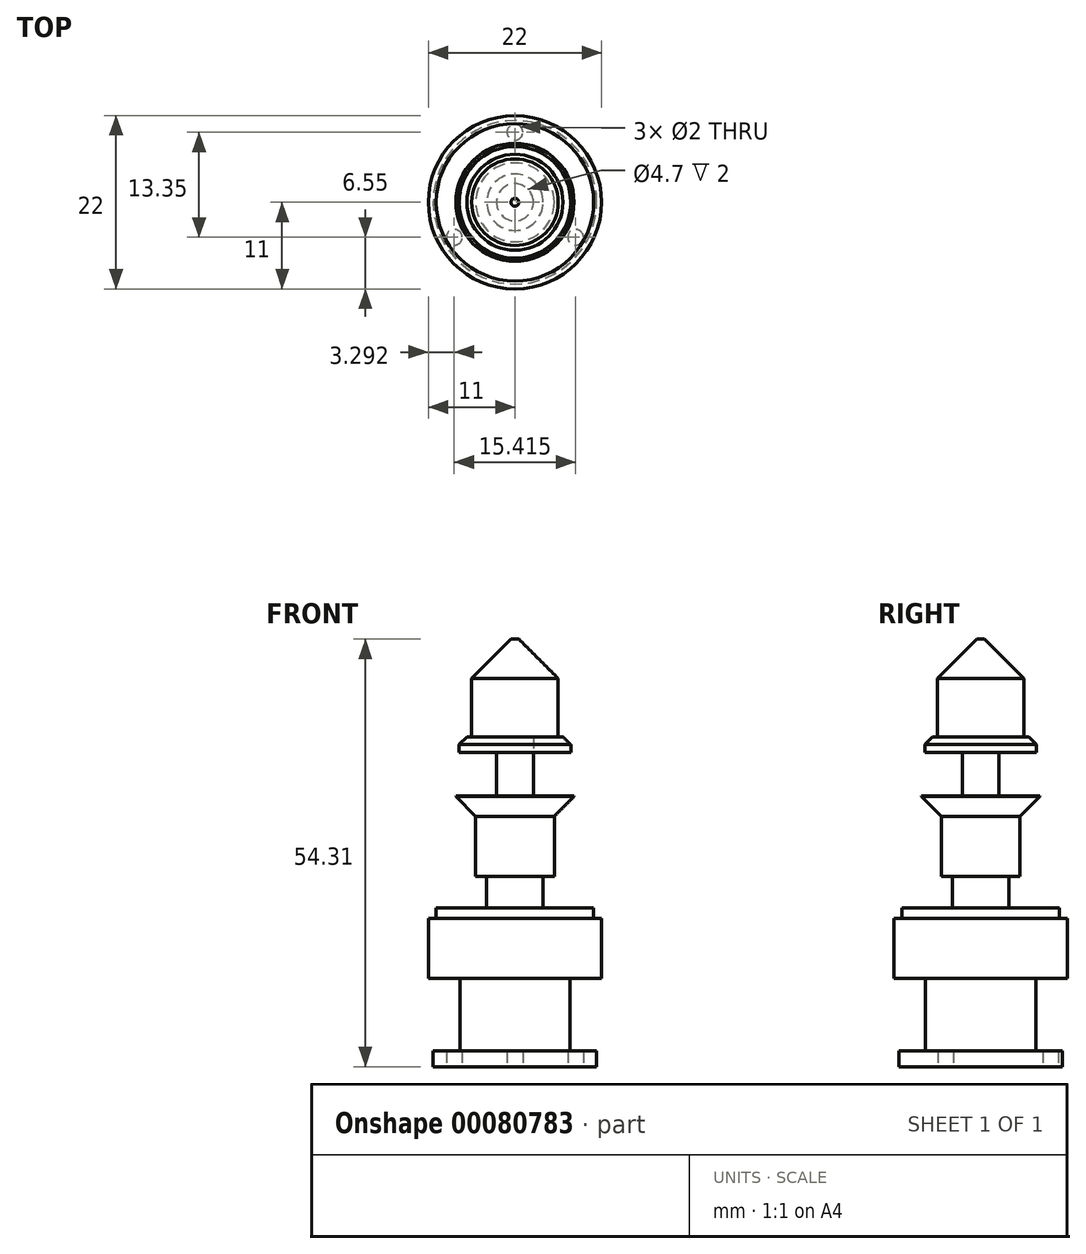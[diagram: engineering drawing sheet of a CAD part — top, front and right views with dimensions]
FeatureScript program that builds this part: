
annotation { "Feature Type Name" : "Feature", "Feature Type Description" : "" }
export const myFeature = defineFeature(function(context is Context, id is Id, definition is map)
    precondition{}
    {
        {
            var Q0;
            Q0=qCreatedBy(makeId("Top.planeOp"),FACE);
            var sketch = newSketch(context, id + "F0", { "sketchPlane" : qUnion([Q0])});
            skCircle(sketch, "E0", {"center": v(0, 0) * mm, "radius": 10.39 * mm});
            skCircle(sketch, "E1", {"center": v(0, 0) * mm, "radius": 8.9 * mm});
            skCircle(sketch, "E2", {"center": v(0, 8.9) * mm, "radius": 1 * mm});
            skCircle(sketch, "E3.1.0", {"center": v(-7.7, -4.45) * mm, "radius": 1 * mm});
            skCircle(sketch, "E3.2.0", {"center": v(7.7, -4.45) * mm, "radius": 1 * mm});
            skSolve(sketch);
        }
        {
            var Q0;
            Q0 = qSketchRegion(id + "F0", true);
            var Q1;
            {var subQ0=sQuery(id+"F0.wireOp",EDGE,"E2");var subQ1=sQuery(id+"F0.wireOp",EDGE,"E1");var subQ2=makeQuery(id+"F0.imprint","INTERSECT",VERTEX,{"disambiguationData":[OD(0.0)],"derivedFrom":[subQ1,subQ0]});Q1=makeQuery(id+"F0.imprint","IMPRINT",FACE,{"disambiguationData":[TD([[makeQuery(id+"F0.imprint","IMPRINT",EDGE,{"disambiguationData":[TD([[subQ2,-1.0]])],"derivedFrom":subQ1}),1.0]])]});}
            extrude(context, id + "F1", {"entities" : qUnion([Q0, Q1]), "depth" : 2 * mm});
        }
        {
            var Q0;
            Q0=makeQuery(id+"F1.opExtrude","CAP_FACE",FACE,{"disambiguationData":[OSD([sQuery(id+"F0.wireOp",EDGE,"E0")])],"isStart":false});
            var sketch = newSketch(context, id + "F2", { "sketchPlane" : qUnion([Q0])});
            skCircle(sketch, "E4", {"center": v(0, 0) * mm, "radius": 7 * mm});
            skSolve(sketch);
        }
        {
            var Q0;
            Q0 = qSketchRegion(id + "F2", true);
            extrude(context, id + "F3", {"entities" : qUnion([Q0]), "operationType" : NewBodyOperationType.ADD, "depth" : 9.2 * mm});
        }
        {
            var Q0;
            Q0=makeQuery(id+"F3.opExtrude","CAP_FACE",FACE,{"disambiguationData":[OSD([sQuery(id+"F2.wireOp",EDGE,"E4")])],"isStart":false});
            var sketch = newSketch(context, id + "F4", { "sketchPlane" : qUnion([Q0])});
            skCircle(sketch, "E5", {"center": v(0, 0) * mm, "radius": 11 * mm});
            skSolve(sketch);
        }
        {
            var Q0;
            Q0=makeQuery(id+"F4.imprint","IMPRINT",FACE,{"disambiguationData":[TD([[makeQuery(id+"F4.imprint","IMPRINT",EDGE,{"derivedFrom":sQuery(id+"F4.wireOp",EDGE,"E5")}),1.0]])]});
            var Q1;
            Q1=makeQuery(id+"F4.imprint","IMPRINT",FACE,{"disambiguationData":[TD([[makeQuery(id+"F4.imprint","IMPRINT",EDGE,{"derivedFrom":makeQuery(id+"F3.opExtrude","CAP_EDGE",EDGE,{"disambiguationData":[OSD([sQuery(id+"F2.wireOp",EDGE,"E4")])],"isStart":false})}),1.0]])]});
            extrude(context, id + "F5", {"entities" : qUnion([Q0, Q1]), "operationType" : NewBodyOperationType.ADD, "depth" : 7.66 * mm});
        }
        {
            var Q0;
            Q0=makeQuery(id+"F5.opExtrude","CAP_FACE",FACE,{"disambiguationData":[OSD([sQuery(id+"F4.wireOp",EDGE,"E5")])],"isStart":false});
            var sketch = newSketch(context, id + "F6", { "sketchPlane" : qUnion([Q0])});
            skCircle(sketch, "E6", {"center": v(0, 0) * mm, "radius": 10 * mm});
            skSolve(sketch);
        }
        {
            var Q0;
            Q0=makeQuery(id+"F6.imprint","IMPRINT",FACE,{"disambiguationData":[TD([[makeQuery(id+"F6.imprint","IMPRINT",EDGE,{"derivedFrom":sQuery(id+"F6.wireOp",EDGE,"E6")}),1.0]])]});
            extrude(context, id + "F7", {"entities" : qUnion([Q0]), "operationType" : NewBodyOperationType.ADD, "depth" : 1.33 * mm});
        }
        {
            var Q0;
            Q0=makeQuery(id+"F7.opExtrude","CAP_FACE",FACE,{"disambiguationData":[OSD([sQuery(id+"F6.wireOp",EDGE,"E6")])],"isStart":false});
            var sketch = newSketch(context, id + "F8", { "sketchPlane" : qUnion([Q0])});
            skCircle(sketch, "E7", {"center": v(0, 0) * mm, "radius": 3.58 * mm});
            skSolve(sketch);
        }
        {
            var Q0;
            Q0 = qSketchRegion(id + "F8", true);
            extrude(context, id + "F9", {"entities" : qUnion([Q0]), "operationType" : NewBodyOperationType.ADD, "depth" : 4 * mm});
        }
        {
            var Q0;
            Q0=makeQuery(id+"F9.opExtrude","CAP_FACE",FACE,{"disambiguationData":[OSD([sQuery(id+"F8.wireOp",EDGE,"E7")])],"isStart":false});
            var sketch = newSketch(context, id + "F10", { "sketchPlane" : qUnion([Q0])});
            skCircle(sketch, "E8", {"center": v(0, 0) * mm, "radius": 5 * mm});
            skSolve(sketch);
        }
        {
            var Q0;
            Q0 = qSketchRegion(id + "F10", true);
            extrude(context, id + "F11", {"entities" : qUnion([Q0]), "operationType" : NewBodyOperationType.ADD, "depth" : 7.62 * mm});
        }
        {
            var Q0;
            Q0=makeQuery(id+"F11.opExtrude","CAP_FACE",FACE,{"disambiguationData":[OSD([sQuery(id+"F10.wireOp",EDGE,"E8")])],"isStart":false});
            var sketch = newSketch(context, id + "F12", { "sketchPlane" : qUnion([Q0])});
            skCircle(sketch, "E9", {"center": v(0, 0) * mm, "radius": 7.5 * mm});
            skSolve(sketch);
        }
        {
            var Q0;
            Q0 = qSketchRegion(id + "F12", true);
            extrude(context, id + "F13", {"entities" : qUnion([Q0]), "operationType" : NewBodyOperationType.ADD, "depth" : 2.6 * mm});
        }
        {
            var Q0;
            Q0=makeQuery(id+"F13.opExtrude","CAP_EDGE",EDGE,{"disambiguationData":[OSD([sQuery(id+"F12.wireOp",EDGE,"E9")])],"isStart":true});
            chamfer(context, id + "F14", {"entities" : qUnion([Q0]), "width" : 2.5 * mm, "tangentPropagation" : true});
        }
        {
            var Q0;
            Q0=makeQuery(id+"F13.opExtrude","CAP_FACE",FACE,{"disambiguationData":[OSD([sQuery(id+"F12.wireOp",EDGE,"E9")])],"isStart":false});
            var sketch = newSketch(context, id + "F15", { "sketchPlane" : qUnion([Q0])});
            skCircle(sketch, "E10", {"center": v(0, 0) * mm, "radius": 2.35 * mm});
            skSolve(sketch);
        }
        {
            var Q0;
            Q0 = qSketchRegion(id + "F15", true);
            extrude(context, id + "F16", {"entities" : qUnion([Q0]), "operationType" : NewBodyOperationType.ADD, "depth" : 5.5 * mm});
        }
        {
            var Q0;
            Q0=makeQuery(id+"F16.opExtrude","CAP_FACE",FACE,{"disambiguationData":[OSD([sQuery(id+"F15.wireOp",EDGE,"E10")])],"isStart":false});
            var sketch = newSketch(context, id + "F17", { "sketchPlane" : qUnion([Q0])});
            skCircle(sketch, "E11", {"center": v(0, 0) * mm, "radius": 7.1 * mm});
            skSolve(sketch);
        }
        {
            var Q0;
            Q0=makeQuery(id+"F17.imprint","IMPRINT",FACE,{"disambiguationData":[TD([[makeQuery(id+"F17.imprint","IMPRINT",EDGE,{"derivedFrom":sQuery(id+"F17.wireOp",EDGE,"E11")}),1.0]])]});
            extrude(context, id + "F18", {"entities" : qUnion([Q0]), "depth" : 2 * mm});
        }
        {
            var Q0;
            Q0=makeQuery(id+"F18.opExtrude","CAP_EDGE",EDGE,{"disambiguationData":[OSD([sQuery(id+"F17.wireOp",EDGE,"E11")])],"isStart":false});
            chamfer(context, id + "F19", {"entities" : qUnion([Q0]), "width" : 1 * mm, "tangentPropagation" : true});
        }
        {
            var Q0;
            Q0=makeQuery(id+"F18.opExtrude","CAP_FACE",FACE,{"disambiguationData":[OSD([sQuery(id+"F15.wireOp",EDGE,"E10"),sQuery(id+"F17.wireOp",EDGE,"E11")])],"isStart":false});
            var sketch = newSketch(context, id + "F20", { "sketchPlane" : qUnion([Q0])});
            skCircle(sketch, "E12", {"center": v(0, 0) * mm, "radius": 5.5 * mm});
            skSolve(sketch);
        }
        {
            var Q0;
            Q0 = qSketchRegion(id + "F20", true);
            extrude(context, id + "F21", {"entities" : qUnion([Q0]), "operationType" : NewBodyOperationType.ADD, "depth" : 12.4 * mm});
        }
        {
            var Q0;
            Q0=makeQuery(id+"F21.opExtrude","CAP_FACE",FACE,{"disambiguationData":[OSD([sQuery(id+"F20.wireOp",EDGE,"E12")])],"isStart":false});
            chamfer(context, id + "F22", {"entities" : qUnion([Q0]), "width" : 5 * mm, "tangentPropagation" : true});
        }
    });
